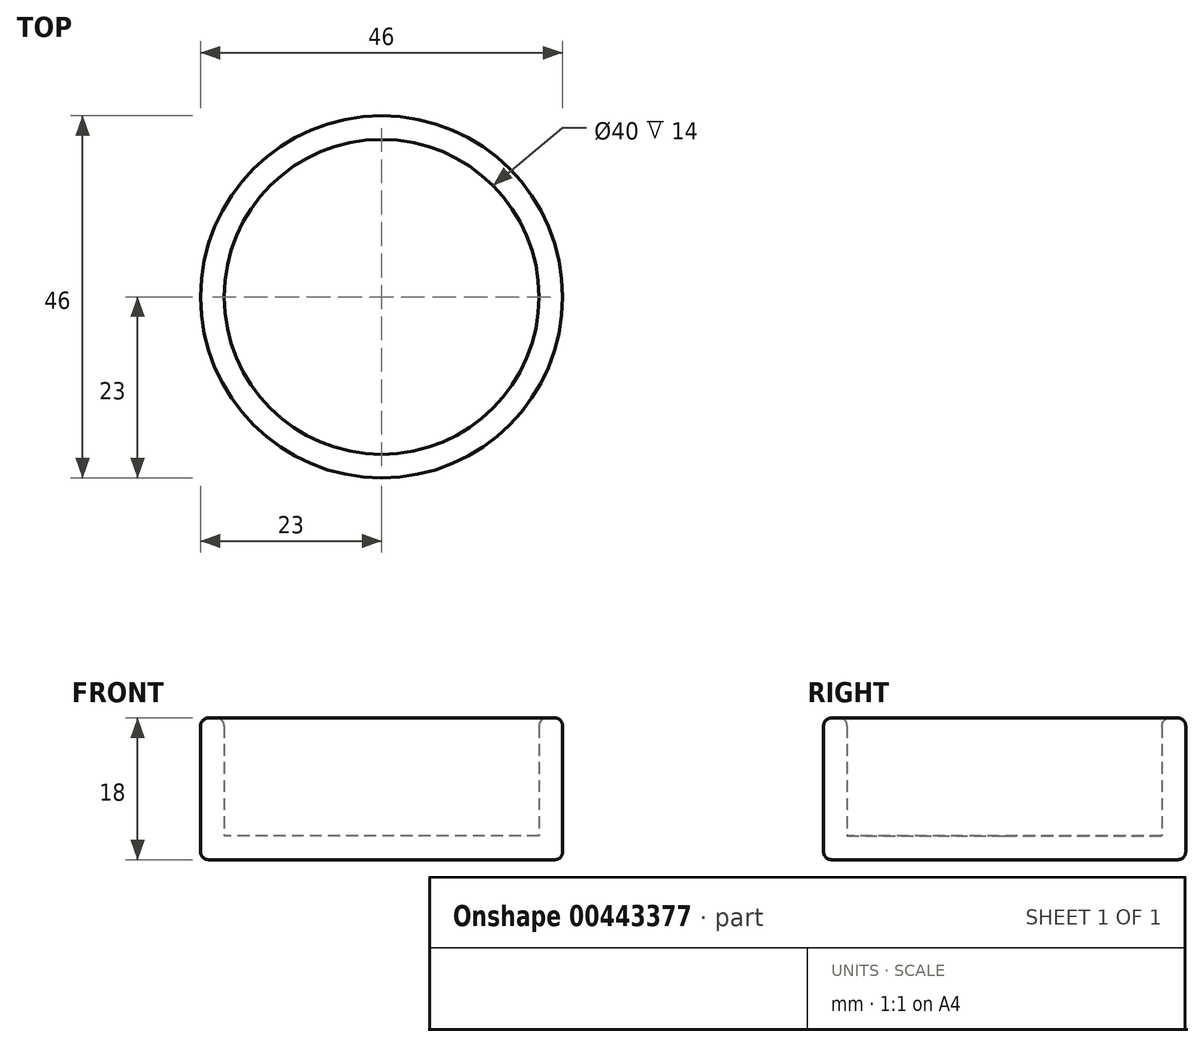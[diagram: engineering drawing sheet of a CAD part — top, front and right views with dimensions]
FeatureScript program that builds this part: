
annotation { "Feature Type Name" : "Feature", "Feature Type Description" : "" }
export const myFeature = defineFeature(function(context is Context, id is Id, definition is map)
    precondition{}
    {
        {
            var Q0;
            Q0=qCreatedBy(makeId("Top.planeOp"),FACE);
            var sketch = newSketch(context, id + "F0", { "sketchPlane" : qUnion([Q0])});
            skCircle(sketch, "E0", {"center": v(0, 0) * mm, "radius": 23 * mm});
            skCircle(sketch, "E1", {"center": v(0, 0) * mm, "radius": 20 * mm});
            skSolve(sketch);
        }
        {
            var Q0;
            Q0=makeQuery(id+"F0.imprint","IMPRINT",FACE,{"disambiguationData":[TD([[makeQuery(id+"F0.imprint","IMPRINT",EDGE,{"derivedFrom":sQuery(id+"F0.wireOp",EDGE,"E0")}),1.0]])]});
            extrude(context, id + "F1", {"entities" : qUnion([Q0]), "depth" : 15 * mm});
        }
        {
            var Q0;
            Q0=qCreatedBy(makeId("Top.planeOp"),FACE);
            var sketch = newSketch(context, id + "F2", { "sketchPlane" : qUnion([Q0])});
            skCircle(sketch, "E2", {"center": v(0, 0) * mm, "radius": 23 * mm});
            skSolve(sketch);
        }
        {
            var Q0;
            Q0 = qSketchRegion(id + "F2", true);
            extrude(context, id + "F3", {"entities" : qUnion([Q0]), "operationType" : NewBodyOperationType.ADD, "oppositeDirection" : true, "depth" : 3 * mm});
        }
        {
            var Q0;
            Q0=makeQuery(id+"F1.opExtrude","CAP_EDGE",EDGE,{"disambiguationData":[OSD([sQuery(id+"F0.wireOp",EDGE,"E0")])],"isStart":false});
            var Q1;
            Q1=makeQuery(id+"F1.opExtrude","CAP_EDGE",EDGE,{"disambiguationData":[OSD([sQuery(id+"F0.wireOp",EDGE,"E1")])],"isStart":false});
            var Q2;
            Q2=makeQuery(id+"F3.boolean.opBoolean","MERGE",FACE,{"derivedFrom":[makeQuery(id+"F1.opExtrude","SWEPT_FACE",FACE,{"disambiguationData":[OSD([sQuery(id+"F0.wireOp",EDGE,"E0")])]}),makeQuery(id+"F3.opExtrude","SWEPT_FACE",FACE,{"disambiguationData":[OSD([sQuery(id+"F2.wireOp",EDGE,"E2")])]})]});
            fillet(context, id + "F4", {"entities" : qUnion([Q0, Q1, Q2]), "radius" : 1 * mm, "tangentPropagation" : true, "allowEdgeOverflow" : false});
        }
    });
